# Revit family: Chiller-Air-Carrier-AquaForce_09FC-(200-400)
name_source: partatom
category: Mechanical Equipment
revit_build: Autodesk Revit 2016 (Build: 20151007_0715(x64)
units: mm (PartAtom-declared; Revit-internal decimal feet)

## family parameters
Always vertical = Yes
Cut with Voids When Loaded = No
OmniClass Number = 23.75.10.24
OmniClass Title = Cooling and Freeze Plant
Part Type = Normal
Room Calculation Point = No
Round Connector Dimension = Use Diameter
Shared = No
Work Plane-Based = Yes

## types (3) — shared parameters
Assembly Code = D3010600
Compressor Type = by Type
Default Elevation = 0' - 0"
Description = Supplemental Air Chiller
Efficiency Ratings = by Type
Height = 8' - 2 15/16"
Keynote = 23 64 26.13
Manufacturer = Carrier
Nominal Capacity = by Type
Operating Temperature Range = -20 to 125 F
Piping Inlet Diameter = 6"
Piping Outlet Diameter = 6"
Product Name = 09FC
Refrigerant Used = by Type
Standards Conformance = by Type
URL = https://www.carrier.com
Width = 7' - 4 1/16"
zero-valued in all types: Integrated Part Load Value

## per-type parameters (varying)
| type | Condenser Set Count | Dead Weight | Frame Length | Length |
| 09FC-040 | 4 | 8098 | 15' - 8 1/4" | 16' - 1 27/32" |
| 09FC-020 | 2 | 4288 | 7' - 10 7/32" | 8' - 3 13/16" |
| 09FC-030 | 3 | 6162 | 11' - 9 7/32" | 12' - 2 13/16" |

note: column(s) folded — value = type name in every type: Model

## geometry (parser evidence)
native form markers: Sweep x5
no freeform markers — native parametric forms only
